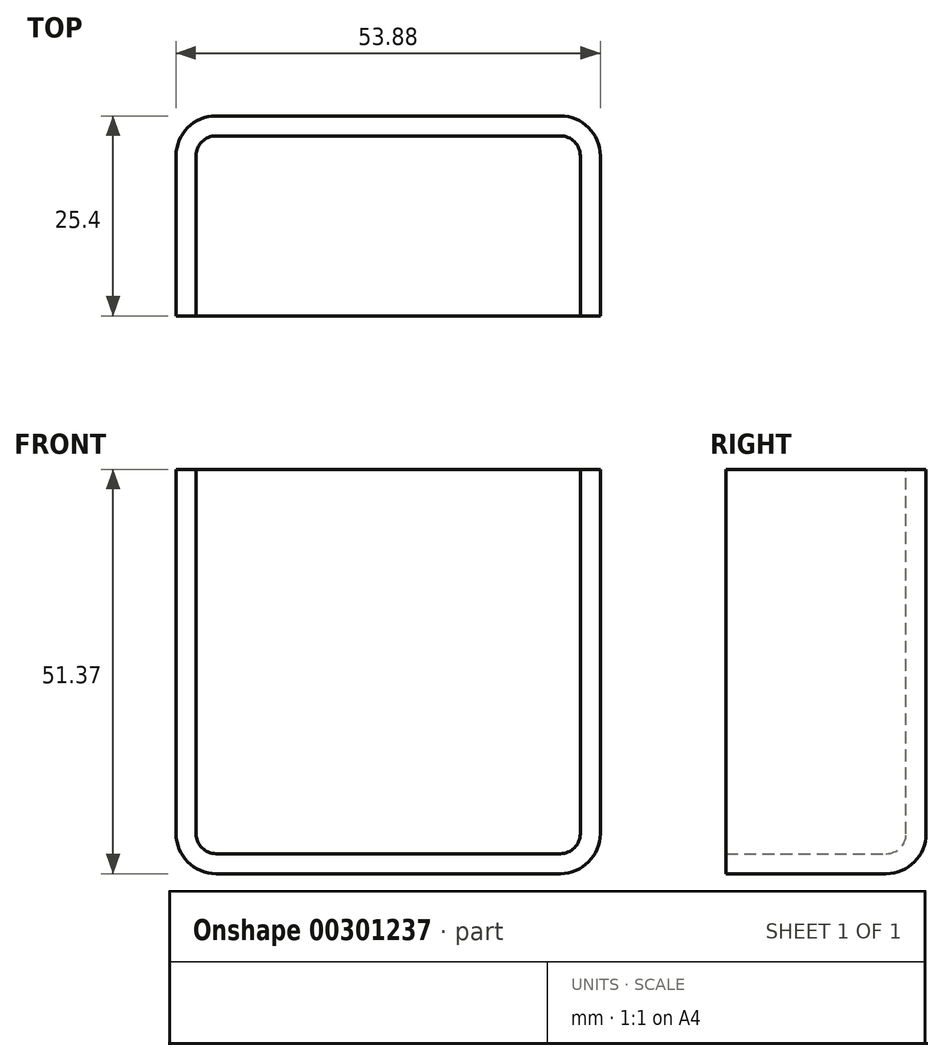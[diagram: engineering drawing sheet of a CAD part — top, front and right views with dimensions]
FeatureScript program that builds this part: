
annotation { "Feature Type Name" : "Feature", "Feature Type Description" : "" }
export const myFeature = defineFeature(function(context is Context, id is Id, definition is map)
    precondition{}
    {
        {
            var Q0;
            Q0=qCreatedBy(makeId("Front.planeOp"),FACE);
            var sketch = newSketch(context, id + "F0", { "sketchPlane" : qUnion([Q0])});
            skLineSegment(sketch, "E0.bottom", {"start": v(-29, 24.58) * mm, "end": v(24.88, 24.58) * mm});
            skLineSegment(sketch, "E0.top", {"start": v(-29, -26.8) * mm, "end": v(24.88, -26.8) * mm});
            skLineSegment(sketch, "E0.left", {"start": v(-29, 24.58) * mm, "end": v(-29, -26.8) * mm});
            skLineSegment(sketch, "E0.right", {"start": v(24.88, 24.58) * mm, "end": v(24.88, -26.8) * mm});
            skSolve(sketch);
        }
        {
            var Q0;
            Q0=makeQuery(id+"F0.imprint","IMPRINT",FACE,{"disambiguationData":[TD([[makeQuery(id+"F0.imprint","IMPRINT",EDGE,{"derivedFrom":sQuery(id+"F0.wireOp",EDGE,"E0.bottom")}),-1.0]])]});
            extrude(context, id + "F1", {"entities" : qUnion([Q0]), "endBound" : BoundingType.SYMMETRIC, "depth" : 25.4 * mm});
        }
        {
            var Q0;
            Q0=makeQuery(id+"F1.opExtrude","SWEPT_EDGE",EDGE,{"disambiguationData":[OSD([sQuery(id+"F0.wireOp",EDGE,"E0.top"),sQuery(id+"F0.wireOp",EDGE,"E0.right")])]});
            var Q1;
            Q1=makeQuery(id+"F1.opExtrude","SWEPT_EDGE",EDGE,{"disambiguationData":[OSD([sQuery(id+"F0.wireOp",EDGE,"E0.top"),sQuery(id+"F0.wireOp",EDGE,"E0.left")])]});
            var Q2;
            Q2=makeQuery(id+"F1.opExtrude","CAP_EDGE",EDGE,{"disambiguationData":[OSD([sQuery(id+"F0.wireOp",EDGE,"E0.left")])],"isStart":true});
            var Q3;
            Q3=makeQuery(id+"F1.opExtrude","CAP_EDGE",EDGE,{"disambiguationData":[OSD([sQuery(id+"F0.wireOp",EDGE,"E0.top")])],"isStart":true});
            var Q4;
            Q4=makeQuery(id+"F1.opExtrude","CAP_EDGE",EDGE,{"disambiguationData":[OSD([sQuery(id+"F0.wireOp",EDGE,"E0.right")])],"isStart":true});
            fillet(context, id + "F2", {"entities" : qUnion([Q0, Q1, Q2, Q3, Q4]), "radius" : 5.08 * mm, "tangentPropagation" : true, "allowEdgeOverflow" : false});
        }
        {
            var Q0;
            Q0=makeQuery(id+"F1.opExtrude","SWEPT_FACE",FACE,{"disambiguationData":[OSD([sQuery(id+"F0.wireOp",EDGE,"E0.bottom")])]});
            var Q1;
            Q1=makeQuery(id+"F1.opExtrude","CAP_FACE",FACE,{"disambiguationData":[OSD([sQuery(id+"F0.wireOp",EDGE,"E0.bottom"),sQuery(id+"F0.wireOp",EDGE,"E0.top"),sQuery(id+"F0.wireOp",EDGE,"E0.left"),sQuery(id+"F0.wireOp",EDGE,"E0.right")])],"isStart":false});
            shell(context, id + "F3", {"entities" : qUnion([Q0, Q1]), "thickness" : 2.54 * mm});
        }
    });
